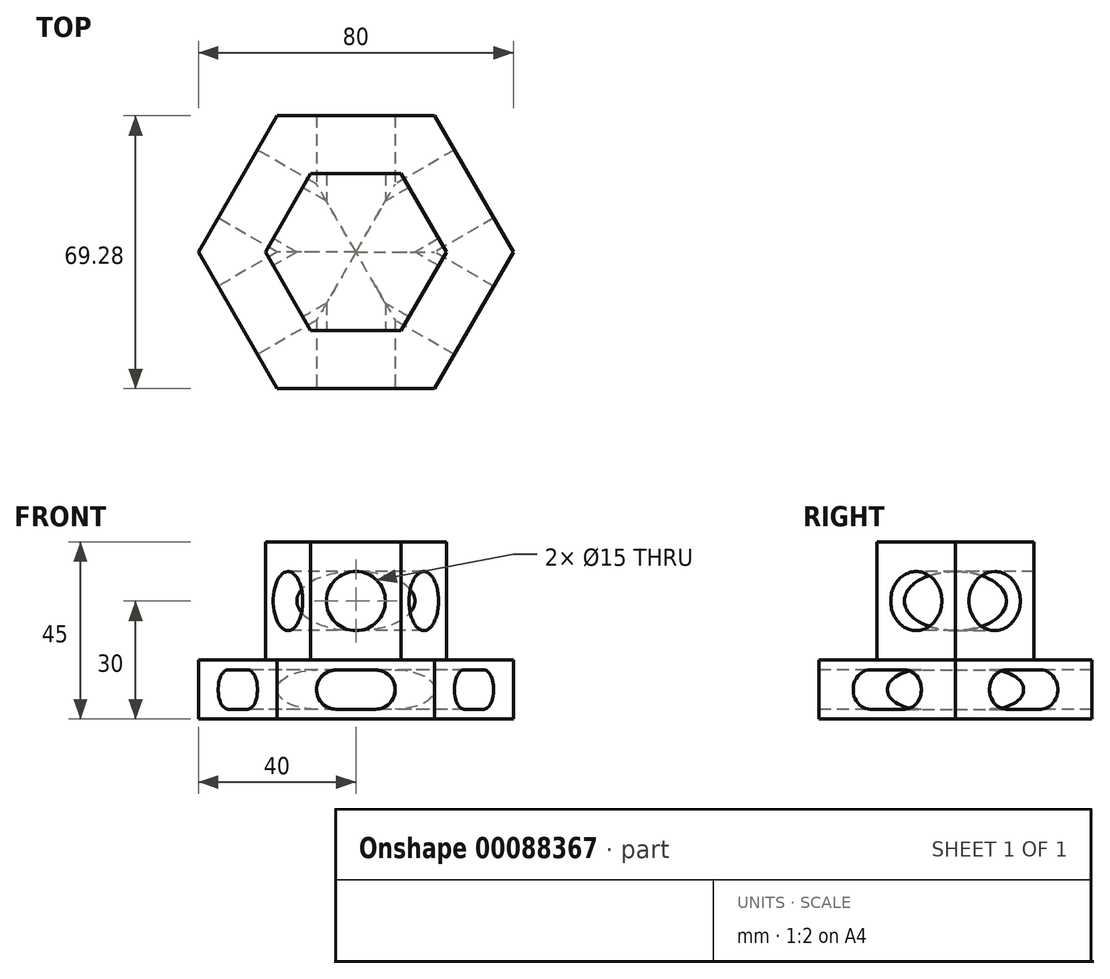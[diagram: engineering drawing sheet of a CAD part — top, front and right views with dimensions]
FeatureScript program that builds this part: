
annotation { "Feature Type Name" : "Feature", "Feature Type Description" : "" }
export const myFeature = defineFeature(function(context is Context, id is Id, definition is map)
    precondition{}
    {
        {
            var Q0;
            Q0=qCreatedBy(makeId("Top.planeOp"),FACE);
            var sketch = newSketch(context, id + "F0", { "sketchPlane" : qUnion([Q0])});
            skLineSegment(sketch, "E0", {"start": v(0, 0) * mm, "end": v(-20, 0) * mm});
            skLineSegment(sketch, "E1", {"start": v(-20, 69.28) * mm, "end": v(0, 69.28) * mm});
            skLineSegment(sketch, "E2", {"start": v(-20, 0) * mm, "end": v(-40, 34.64) * mm});
            skLineSegment(sketch, "E3", {"start": v(-40, 34.64) * mm, "end": v(-20, 69.28) * mm});
            skLineSegment(sketch, "E4.MirrorCS", {"start": v(40, 34.64) * mm, "end": v(20, 69.28) * mm});
            skLineSegment(sketch, "E5.MirrorCS", {"start": v(20, 69.28) * mm, "end": v(0, 69.28) * mm});
            skLineSegment(sketch, "E6.MirrorCS", {"start": v(20, 0) * mm, "end": v(40, 34.64) * mm});
            skLineSegment(sketch, "E7.MirrorCS", {"start": v(0, 0) * mm, "end": v(20, 0) * mm});
            skLineSegment(sketch, "E8.0", {"start": v(0, 14.72) * mm, "end": v(11.5, 14.72) * mm, "construction": true});
            skLineSegment(sketch, "E8.1", {"start": v(0, 14.72) * mm, "end": v(-11.5, 14.72) * mm, "construction": true});
            skLineSegment(sketch, "E8.2", {"start": v(11.5, 14.72) * mm, "end": v(23, 34.64) * mm, "construction": true});
            skLineSegment(sketch, "E8.3", {"start": v(-11.5, 14.72) * mm, "end": v(-23, 34.64) * mm, "construction": true});
            skLineSegment(sketch, "E8.4", {"start": v(23, 34.64) * mm, "end": v(11.5, 54.56) * mm, "construction": true});
            skLineSegment(sketch, "E8.5", {"start": v(11.5, 54.56) * mm, "end": v(5.45, 54.56) * mm, "construction": true});
            skLineSegment(sketch, "E8.6", {"start": v(-11.5, 54.56) * mm, "end": v(5.45, 54.56) * mm, "construction": true});
            skLineSegment(sketch, "E8.7", {"start": v(-23, 34.64) * mm, "end": v(-11.5, 54.56) * mm, "construction": true});
            skSolve(sketch);
        }
        {
            var Q0;
            Q0 = qSketchRegion(id + "F0", true);
            extrude(context, id + "F1", {"entities" : qUnion([Q0]), "oppositeDirection" : true, "depth" : 15 * mm});
        }
        {
            var Q0;
            Q0=makeQuery(id+"F1.opExtrude","SWEPT_FACE",FACE,{"disambiguationData":[OSD([sQuery(id+"F0.wireOp",EDGE,"E2")])]});
            var sketch = newSketch(context, id + "F2", { "sketchPlane" : qUnion([Q0])});
            skLineSegment(sketch, "E9", {"start": v(-30, 0) * mm, "end": v(-30, -15) * mm, "construction": true});
            skLineSegment(sketch, "E10", {"start": v(-10, -7.5) * mm, "end": v(-50, -7.5) * mm, "construction": true});
            skLineSegment(sketch, "E11", {"start": v(-35, -7.5) * mm, "end": v(-25, -7.5) * mm, "construction": true});
            skArc(sketch, "E12.0.startCap", {"start": v(-35, -12.5) * mm, "mid": v(-40, -7.5) * mm, "end": v(-35, -2.5) * mm});
            skArc(sketch, "E12.0.endCap", {"start": v(-25, -2.5) * mm, "mid": v(-20, -7.5) * mm, "end": v(-25, -12.5) * mm});
            skLineSegment(sketch, "E12.0.left", {"start": v(-35, -2.5) * mm, "end": v(-25, -2.5) * mm});
            skLineSegment(sketch, "E12.0.right", {"start": v(-35, -12.5) * mm, "end": v(-25, -12.5) * mm});
            skSolve(sketch);
        }
        {
            var Q0;
            Q0=makeQuery(id+"F1.opExtrude","SWEPT_FACE",FACE,{"disambiguationData":[OSD([sQuery(id+"F0.wireOp",EDGE,"E3")])]});
            var sketch = newSketch(context, id + "F3", { "sketchPlane" : qUnion([Q0])});
            skLineSegment(sketch, "E13", {"start": v(-30, 0) * mm, "end": v(-30, -15) * mm, "construction": true});
            skLineSegment(sketch, "E14", {"start": v(-25, -7.5) * mm, "end": v(-35, -7.5) * mm, "construction": true});
            skPoint(sketch, "E14.startSnap0", {"position": v(-10, -7.5) * mm});
            skArc(sketch, "E15.0.startCap", {"start": v(-25, -2.5) * mm, "mid": v(-20, -7.5) * mm, "end": v(-25, -12.5) * mm});
            skArc(sketch, "E15.0.endCap", {"start": v(-35, -12.5) * mm, "mid": v(-40, -7.5) * mm, "end": v(-35, -2.5) * mm});
            skLineSegment(sketch, "E15.0.left", {"start": v(-25, -12.5) * mm, "end": v(-35, -12.5) * mm});
            skLineSegment(sketch, "E15.0.right", {"start": v(-25, -2.5) * mm, "end": v(-35, -2.5) * mm});
            skSolve(sketch);
        }
        {
            var Q0;
            Q0 = qSketchRegion(id + "F3", true);
            extrude(context, id + "F4", {"entities" : qUnion([Q0]), "operationType" : NewBodyOperationType.REMOVE, "oppositeDirection" : true, "depth" : 80 * mm});
        }
        {
            var Q0;
            Q0=makeQuery(id+"F1.opExtrude","SWEPT_FACE",FACE,{"disambiguationData":[OSD([sQuery(id+"F0.wireOp",EDGE,"E0"),sQuery(id+"F0.wireOp",EDGE,"E7.MirrorCS")])]});
            var sketch = newSketch(context, id + "F5", { "sketchPlane" : qUnion([Q0])});
            skLineSegment(sketch, "E16", {"start": v(0, -15) * mm, "end": v(0, 0) * mm, "construction": true});
            skLineSegment(sketch, "E17", {"start": v(0, -7.5) * mm, "end": v(5, -7.5) * mm, "construction": true});
            skLineSegment(sketch, "E18.MirrorCS", {"start": v(0, -7.5) * mm, "end": v(-5, -7.5) * mm, "construction": true});
            skLineSegment(sketch, "E19", {"start": v(5, -7.5) * mm, "end": v(-5, -7.5) * mm, "construction": true});
            skArc(sketch, "E20.0.startCap", {"start": v(5, -2.5) * mm, "mid": v(10, -7.5) * mm, "end": v(5, -12.5) * mm});
            skArc(sketch, "E20.0.endCap", {"start": v(-5, -12.5) * mm, "mid": v(-10, -7.5) * mm, "end": v(-5, -2.5) * mm});
            skLineSegment(sketch, "E20.0.left", {"start": v(5, -12.5) * mm, "end": v(-5, -12.5) * mm});
            skLineSegment(sketch, "E20.0.right", {"start": v(5, -2.5) * mm, "end": v(-5, -2.5) * mm});
            skSolve(sketch);
        }
        {
            var Q0;
            Q0 = qSketchRegion(id + "F5", true);
            extrude(context, id + "F6", {"entities" : qUnion([Q0]), "operationType" : NewBodyOperationType.REMOVE, "oppositeDirection" : true, "depth" : 80 * mm});
        }
        {
            var Q0;
            Q0 = qSketchRegion(id + "F2", true);
            extrude(context, id + "F7", {"entities" : qUnion([Q0]), "operationType" : NewBodyOperationType.REMOVE, "oppositeDirection" : true, "depth" : 80 * mm});
        }
        {
            var Q0;
            Q0=makeQuery(id+"F1.opExtrude","CAP_FACE",FACE,{"disambiguationData":[OSD([sQuery(id+"F0.wireOp",EDGE,"E0"),sQuery(id+"F0.wireOp",EDGE,"E1"),sQuery(id+"F0.wireOp",EDGE,"E2"),sQuery(id+"F0.wireOp",EDGE,"E3"),sQuery(id+"F0.wireOp",EDGE,"E4.MirrorCS"),sQuery(id+"F0.wireOp",EDGE,"E5.MirrorCS"),sQuery(id+"F0.wireOp",EDGE,"E6.MirrorCS"),sQuery(id+"F0.wireOp",EDGE,"E7.MirrorCS")])],"isStart":true});
            var sketch = newSketch(context, id + "F8", { "sketchPlane" : qUnion([Q0])});
            skLineSegment(sketch, "E21", {"start": v(-11.5, 54.56) * mm, "end": v(11.5, 54.56) * mm});
            skLineSegment(sketch, "E22", {"start": v(11.5, 54.56) * mm, "end": v(23, 34.64) * mm});
            skLineSegment(sketch, "E23", {"start": v(23, 34.64) * mm, "end": v(11.5, 14.72) * mm});
            skLineSegment(sketch, "E24", {"start": v(11.5, 14.72) * mm, "end": v(-11.5, 14.72) * mm});
            skLineSegment(sketch, "E25", {"start": v(-11.5, 14.72) * mm, "end": v(-23, 34.64) * mm});
            skLineSegment(sketch, "E26", {"start": v(-23, 34.64) * mm, "end": v(-11.5, 54.56) * mm});
            skLineSegment(sketch, "E27", {"start": v(0, 54.56) * mm, "end": v(0, 14.72) * mm, "construction": true});
            skLineSegment(sketch, "E28", {"start": v(-23, 34.64) * mm, "end": v(23, 34.64) * mm, "construction": true});
            skSolve(sketch);
        }
        {
            var Q0;
            Q0 = qSketchRegion(id + "F8", true);
            extrude(context, id + "F9", {"entities" : qUnion([Q0]), "operationType" : NewBodyOperationType.ADD, "depth" : 30 * mm});
        }
        {
            var Q0;
            Q0=makeQuery(id+"F9.opExtrude","SWEPT_FACE",FACE,{"disambiguationData":[OSD([sQuery(id+"F8.wireOp",EDGE,"E24")])]});
            var sketch = newSketch(context, id + "F10", { "sketchPlane" : qUnion([Q0])});
            skPoint(sketch, "E29", {"position": v(0, 15) * mm});
            skPoint(sketch, "E29.positionSnap0", {"position": v(0, 30) * mm});
            skLineSegment(sketch, "E30", {"start": v(0, 30) * mm, "end": v(0, 0) * mm, "construction": true});
            skSolve(sketch);
        }
        {
            var Q0;
            Q0=sQuery(id+"F10.wireOp",VERTEX,"E29");
            var Q1;
            Q1=makeQuery(id+"F1.opExtrude","SWEPT_BODY",BODY,{"disambiguationData":[OSD([sQuery(id+"F0.wireOp",EDGE,"E0"),sQuery(id+"F0.wireOp",EDGE,"E1"),sQuery(id+"F0.wireOp",EDGE,"E2"),sQuery(id+"F0.wireOp",EDGE,"E3"),sQuery(id+"F0.wireOp",EDGE,"E4.MirrorCS"),sQuery(id+"F0.wireOp",EDGE,"E5.MirrorCS"),sQuery(id+"F0.wireOp",EDGE,"E6.MirrorCS"),sQuery(id+"F0.wireOp",EDGE,"E7.MirrorCS")])]});
            hole(context, id + "F11", {"style" : HoleStyle.SIMPLE, "endStyle" : HoleEndStyle.BLIND, "holeDiameter" : 15 * mm, "holeDepth" : 80 * mm, "startFromSketch" : true, "locations" : qUnion([Q0]), "scope" : qUnion([Q1])});
        }
        {
            var Q0;
            Q0=makeQuery(id+"F9.opExtrude","SWEPT_FACE",FACE,{"disambiguationData":[OSD([sQuery(id+"F8.wireOp",EDGE,"E25")])]});
            var sketch = newSketch(context, id + "F12", { "sketchPlane" : qUnion([Q0])});
            skLineSegment(sketch, "E31", {"start": v(-30, 30) * mm, "end": v(-30, 0) * mm, "construction": true});
            skPoint(sketch, "E32", {"position": v(-30, 15) * mm});
            skSolve(sketch);
        }
        {
            var Q0;
            Q0=makeQuery(id+"F9.opExtrude","SWEPT_FACE",FACE,{"disambiguationData":[OSD([sQuery(id+"F8.wireOp",EDGE,"E26")])]});
            var sketch = newSketch(context, id + "F13", { "sketchPlane" : qUnion([Q0])});
            skLineSegment(sketch, "E33", {"start": v(-30, 30) * mm, "end": v(-30, 0) * mm, "construction": true});
            skPoint(sketch, "E34", {"position": v(-30, 15) * mm});
            skSolve(sketch);
        }
        {
            var Q0;
            Q0=sQuery(id+"F12.wireOp",VERTEX,"E32");
            var Q1;
            Q1=makeQuery(id+"F1.opExtrude","SWEPT_BODY",BODY,{"disambiguationData":[OSD([sQuery(id+"F0.wireOp",EDGE,"E0"),sQuery(id+"F0.wireOp",EDGE,"E1"),sQuery(id+"F0.wireOp",EDGE,"E2"),sQuery(id+"F0.wireOp",EDGE,"E3"),sQuery(id+"F0.wireOp",EDGE,"E4.MirrorCS"),sQuery(id+"F0.wireOp",EDGE,"E5.MirrorCS"),sQuery(id+"F0.wireOp",EDGE,"E6.MirrorCS"),sQuery(id+"F0.wireOp",EDGE,"E7.MirrorCS")])]});
            hole(context, id + "F14", {"style" : HoleStyle.SIMPLE, "endStyle" : HoleEndStyle.BLIND, "holeDiameter" : 15 * mm, "holeDepth" : 80 * mm, "startFromSketch" : true, "locations" : qUnion([Q0]), "scope" : qUnion([Q1])});
        }
        {
            var Q0;
            Q0=sQuery(id+"F13.wireOp",VERTEX,"E34");
            var Q1;
            Q1=makeQuery(id+"F1.opExtrude","SWEPT_BODY",BODY,{"disambiguationData":[OSD([sQuery(id+"F0.wireOp",EDGE,"E0"),sQuery(id+"F0.wireOp",EDGE,"E1"),sQuery(id+"F0.wireOp",EDGE,"E2"),sQuery(id+"F0.wireOp",EDGE,"E3"),sQuery(id+"F0.wireOp",EDGE,"E4.MirrorCS"),sQuery(id+"F0.wireOp",EDGE,"E5.MirrorCS"),sQuery(id+"F0.wireOp",EDGE,"E6.MirrorCS"),sQuery(id+"F0.wireOp",EDGE,"E7.MirrorCS")])]});
            hole(context, id + "F15", {"style" : HoleStyle.SIMPLE, "endStyle" : HoleEndStyle.BLIND, "holeDiameter" : 15 * mm, "holeDepth" : 80 * mm, "startFromSketch" : true, "locations" : qUnion([Q0]), "scope" : qUnion([Q1])});
        }
    });
